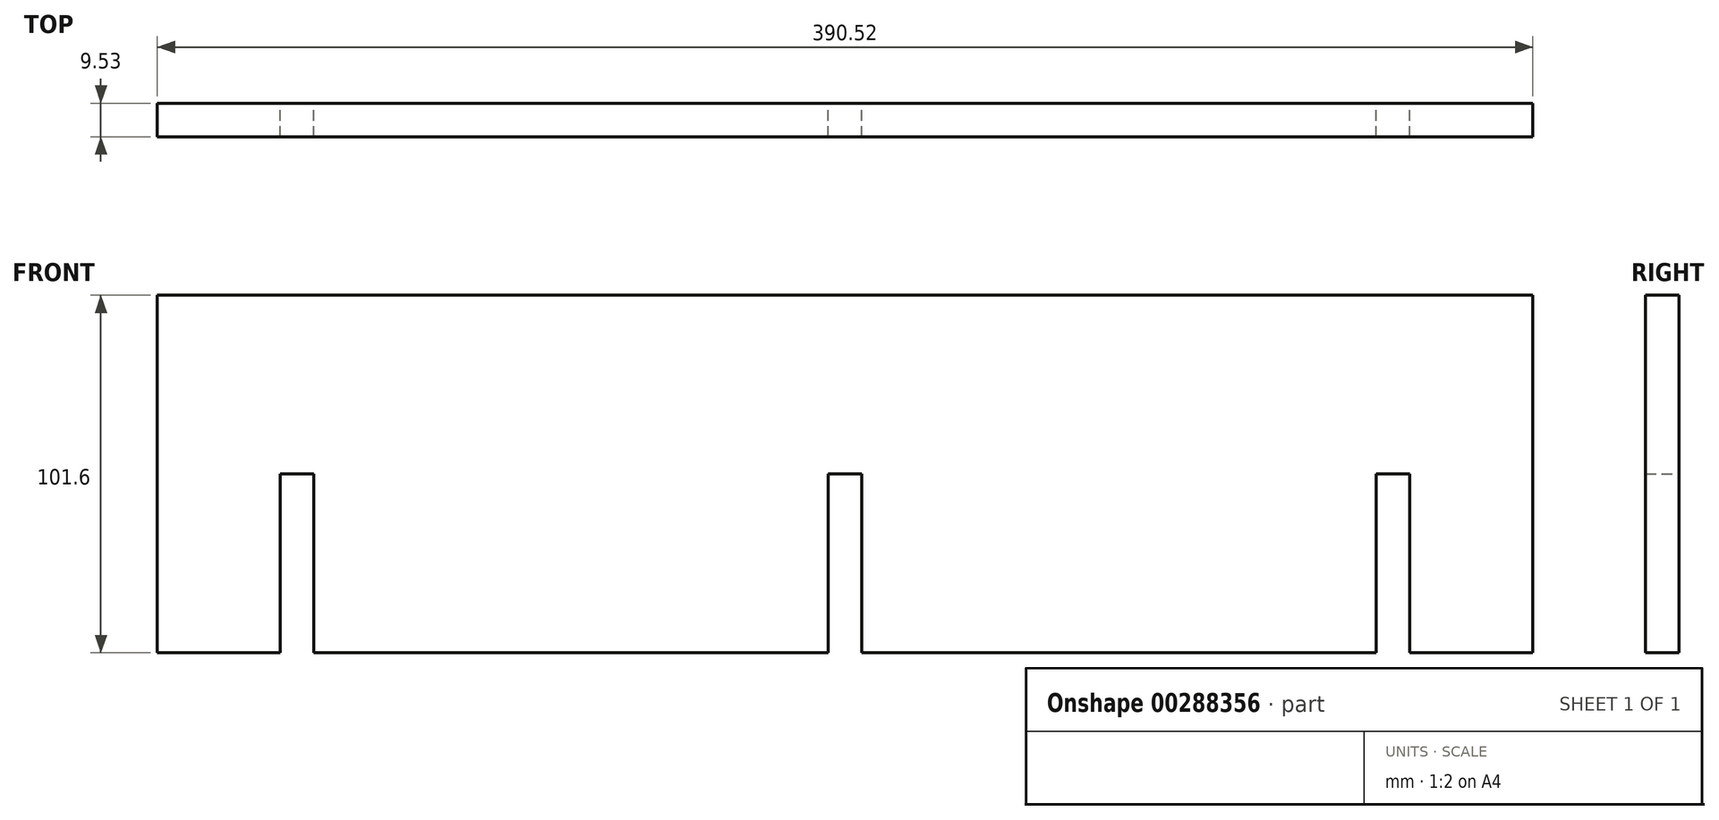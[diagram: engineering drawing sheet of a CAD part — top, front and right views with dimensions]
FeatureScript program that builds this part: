
annotation { "Feature Type Name" : "Feature", "Feature Type Description" : "" }
export const myFeature = defineFeature(function(context is Context, id is Id, definition is map)
    precondition{}
    {
        {
            var Q0;
            Q0=qCreatedBy(makeId("Front.planeOp"),FACE);
            var sketch = newSketch(context, id + "F0", { "sketchPlane" : qUnion([Q0])});
            skLineSegment(sketch, "E0.bottom", {"start": v(-195.26, -50.8) * mm, "end": v(-160.34, -50.8) * mm});
            skLineSegment(sketch, "E0.top", {"start": v(-195.26, 50.8) * mm, "end": v(195.26, 50.8) * mm});
            skLineSegment(sketch, "E0.left", {"start": v(-195.26, -50.8) * mm, "end": v(-195.26, 50.8) * mm});
            skLineSegment(sketch, "E0.right", {"start": v(195.26, -50.8) * mm, "end": v(195.26, 50.8) * mm});
            skPoint(sketch, "E0.middle", {"position": v(0, 0) * mm});
            skLineSegment(sketch, "E1.top", {"start": v(-160.34, 0) * mm, "end": v(-150.81, 0) * mm});
            skLineSegment(sketch, "E1.left", {"start": v(-160.34, -50.8) * mm, "end": v(-160.34, 0) * mm});
            skLineSegment(sketch, "E1.right", {"start": v(-150.81, -50.8) * mm, "end": v(-150.81, 0) * mm});
            skLineSegment(sketch, "E2.top", {"start": v(160.34, 0) * mm, "end": v(150.81, 0) * mm});
            skLineSegment(sketch, "E2.left", {"start": v(160.34, -50.8) * mm, "end": v(160.34, 0) * mm});
            skLineSegment(sketch, "E2.right", {"start": v(150.81, -50.8) * mm, "end": v(150.81, 0) * mm});
            skPoint(sketch, "E3.oppositeSnap0", {"position": v(160.34, -25.4) * mm});
            skLineSegment(sketch, "E3.left", {"start": v(160.34, -25.4) * mm, "end": v(160.34, -25.4) * mm});
            skLineSegment(sketch, "E3.right", {"start": v(195.26, -25.4) * mm, "end": v(195.26, -25.4) * mm});
            skLineSegment(sketch, "E4.trimOffspring", {"start": v(-150.81, -50.8) * mm, "end": v(-4.76, -50.8) * mm});
            skLineSegment(sketch, "E5.trimOffspring", {"start": v(160.34, -50.8) * mm, "end": v(195.26, -50.8) * mm});
            skLineSegment(sketch, "E6.top", {"start": v(-6.92, 0) * mm, "end": v(2.6, 0) * mm});
            skLineSegment(sketch, "E7.top", {"start": v(-4.76, 0) * mm, "end": v(4.76, 0) * mm});
            skLineSegment(sketch, "E7.left", {"start": v(-4.76, -50.8) * mm, "end": v(-4.76, 0) * mm});
            skLineSegment(sketch, "E7.right", {"start": v(4.76, -50.8) * mm, "end": v(4.76, 0) * mm});
            skLineSegment(sketch, "E8.trimOffspring", {"start": v(4.76, -50.8) * mm, "end": v(150.81, -50.8) * mm});
            skSolve(sketch);
        }
        {
            var Q0;
            Q0 = qSketchRegion(id + "F0", true);
            extrude(context, id + "F1", {"entities" : qUnion([Q0]), "depth" : 9.52 * mm});
        }
    });
